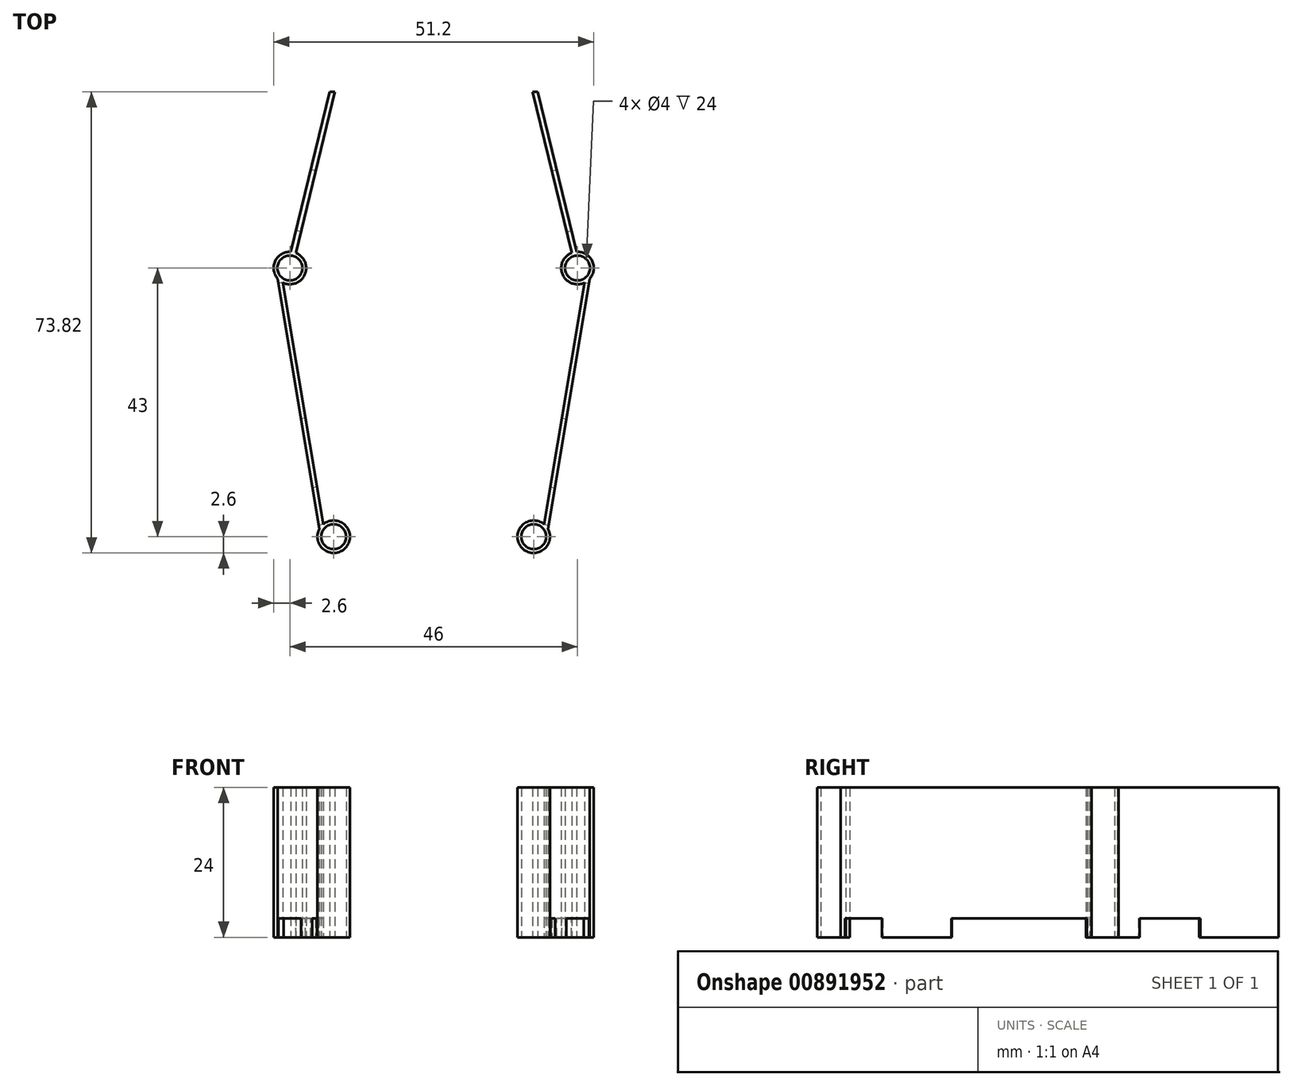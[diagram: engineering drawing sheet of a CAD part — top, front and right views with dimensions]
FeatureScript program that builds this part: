
annotation { "Feature Type Name" : "Feature", "Feature Type Description" : "" }
export const myFeature = defineFeature(function(context is Context, id is Id, definition is map)
    precondition{}
    {
        {
            var Q0;
            Q0=qCreatedBy(makeId("Top.planeOp"),FACE);
            var sketch = newSketch(context, id + "F0", { "sketchPlane" : qUnion([Q0])});
            skCircle(sketch, "E0", {"center": v(-23, 43) * mm, "radius": 2.6 * mm});
            skCircle(sketch, "E1", {"center": v(-16, 0) * mm, "radius": 2.6 * mm});
            skSolve(sketch);
        }
        {
            var Q0;
            Q0=qSketchRegion(id+"F0",true);
            extrude(context, id + "F1", {"entities" : qUnion([Q0]), "depth" : 24 * mm});
        }
        {
            var Q0;
            Q0=qCreatedBy(makeId("Top.planeOp"),FACE);
            var sketch = newSketch(context, id + "F2", { "sketchPlane" : qUnion([Q0])});
            skCircle(sketch, "E2", {"center": v(-13, 85.6) * mm, "radius": 3.12 * mm});
            skSolve(sketch);
        }
        {
            var Q0;
            Q0=qCreatedBy(makeId("Top.planeOp"),FACE);
            var sketch = newSketch(context, id + "F3", { "sketchPlane" : qUnion([Q0])});
            skLineSegment(sketch, "E3", {"start": v(-25.3, 43.5) * mm, "end": v(-18.12, 0) * mm});
            skLineSegment(sketch, "E4", {"start": v(-18.12, 0) * mm, "end": v(-17.32, 0) * mm});
            skLineSegment(sketch, "E5", {"start": v(-17.32, 0) * mm, "end": v(-24.73, 44.05) * mm});
            skLineSegment(sketch, "E6", {"start": v(-25.3, 43.5) * mm, "end": v(-25.3, 43.5) * mm});
            skLineSegment(sketch, "E7", {"start": v(-25.3, 43.5) * mm, "end": v(-24.73, 44.05) * mm});
            skLineSegment(sketch, "E8", {"start": v(-23.3, 43.66) * mm, "end": v(-16.64, 71.22) * mm});
            skLineSegment(sketch, "E9", {"start": v(-15.84, 71.22) * mm, "end": v(-22.5, 43.61) * mm});
            skLineSegment(sketch, "E10", {"start": v(-16.64, 71.22) * mm, "end": v(-15.84, 71.22) * mm});
            skLineSegment(sketch, "E11", {"start": v(-23.3, 43.66) * mm, "end": v(-22.5, 43.61) * mm});
            skSolve(sketch);
        }
        {
            var Q0;
            Q0=qSketchRegion(id+"F3",true);
            extrude(context, id + "F4", {"entities" : qUnion([Q0]), "operationType" : NewBodyOperationType.ADD, "depth" : 24 * mm});
        }
        {
            var Q0;
            Q0=sQuery(id+"F0.wireOp",VERTEX,"E0.center");
            var Q1;
            Q1=sQuery(id+"F0.wireOp",VERTEX,"E1.center");
            var Q2;
            Q2=makeQuery(id+"F1.opExtrude","SWEPT_BODY",BODY,{"disambiguationData":[OSD([sQuery(id+"F0.wireOp",EDGE,"E0")])]});
            hole(context, id + "F5", {"style" : HoleStyle.SIMPLE, "endStyle" : HoleEndStyle.THROUGH, "oppositeDirection" : true, "holeDiameter" : 4 * mm, "isTappedThrough" : true, "tappedDepth" : 12 * mm, "tapClearance" : 3, "locations" : qUnion([Q0, Q1]), "scope" : qUnion([Q2])});
        }
        {
            var Q0;
            Q0=makeQuery(id+"F4.opExtrude","SWEPT_FACE",FACE,{"disambiguationData":[OSD([sQuery(id+"F3.wireOp",EDGE,"E3")])]});
            var sketch = newSketch(context, id + "F6", { "sketchPlane" : qUnion([Q0])});
            skLineSegment(sketch, "E12", {"start": v(-44.07, 0) * mm, "end": v(-22.07, 0) * mm});
            skLineSegment(sketch, "E13", {"start": v(-22.07, 0) * mm, "end": v(-22.07, 3) * mm});
            skLineSegment(sketch, "E14", {"start": v(-44.07, 3) * mm, "end": v(-44.07, 0) * mm});
            skLineSegment(sketch, "E15.top", {"start": v(-4.86, 0) * mm, "end": v(-10.86, 0) * mm});
            skLineSegment(sketch, "E15.left", {"start": v(-4.86, 3) * mm, "end": v(-4.86, 0) * mm});
            skLineSegment(sketch, "E15.right", {"start": v(-10.86, 3) * mm, "end": v(-10.86, 0) * mm});
            skLineSegment(sketch, "E16", {"start": v(-44.07, 3) * mm, "end": v(-22.07, 3) * mm});
            skLineSegment(sketch, "E17", {"start": v(-10.86, 3) * mm, "end": v(-4.86, 3) * mm});
            skSolve(sketch);
        }
        {
            var Q0;
            Q0=makeQuery(id+"F6.imprint","IMPRINT",FACE,{"disambiguationData":[TD([[makeQuery(id+"F6.imprint","IMPRINT",EDGE,{"derivedFrom":sQuery(id+"F6.wireOp",EDGE,"E12")}),1.0]])]});
            var Q1;
            Q1=makeQuery(id+"F6.imprint","IMPRINT",FACE,{"disambiguationData":[TD([[makeQuery(id+"F6.imprint","IMPRINT",EDGE,{"derivedFrom":sQuery(id+"F6.wireOp",EDGE,"E15.top")}),1.0]])]});
            extrude(context, id + "F7", {"entities" : qUnion([Q0, Q1]), "operationType" : NewBodyOperationType.REMOVE, "oppositeDirection" : true, "depth" : 0.8 * mm});
        }
        {
            var Q0;
            Q0=makeQuery(id+"F4.opExtrude","SWEPT_FACE",FACE,{"disambiguationData":[OSD([sQuery(id+"F3.wireOp",EDGE,"E8")])]});
            var sketch = newSketch(context, id + "F8", { "sketchPlane" : qUnion([Q0])});
            skLineSegment(sketch, "E18.bottom", {"start": v(-52.45, 0) * mm, "end": v(-42.45, 0) * mm});
            skLineSegment(sketch, "E18.top", {"start": v(-52.45, 3) * mm, "end": v(-42.45, 3) * mm});
            skLineSegment(sketch, "E18.left", {"start": v(-52.45, 0) * mm, "end": v(-52.45, 3) * mm});
            skLineSegment(sketch, "E18.right", {"start": v(-42.45, 0) * mm, "end": v(-42.45, 3) * mm});
            skSolve(sketch);
        }
        {
            var Q0;
            Q0=qSketchRegion(id+"F8",true);
            extrude(context, id + "F9", {"entities" : qUnion([Q0]), "operationType" : NewBodyOperationType.REMOVE, "oppositeDirection" : true, "depth" : 2 * mm});
        }
        {
            var Q0;
            Q0=makeQuery(id+"F1.opExtrude","SWEPT_BODY",BODY,{"disambiguationData":[OSD([sQuery(id+"F0.wireOp",EDGE,"E0")])]});
            var Q1;
            Q1=qCreatedBy(makeId("Right.planeOp"),FACE);
            mirror(context, id + "F10", {"entities" : qUnion([Q0]), "mirrorPlane" : qUnion([Q1])});
        }
    });
